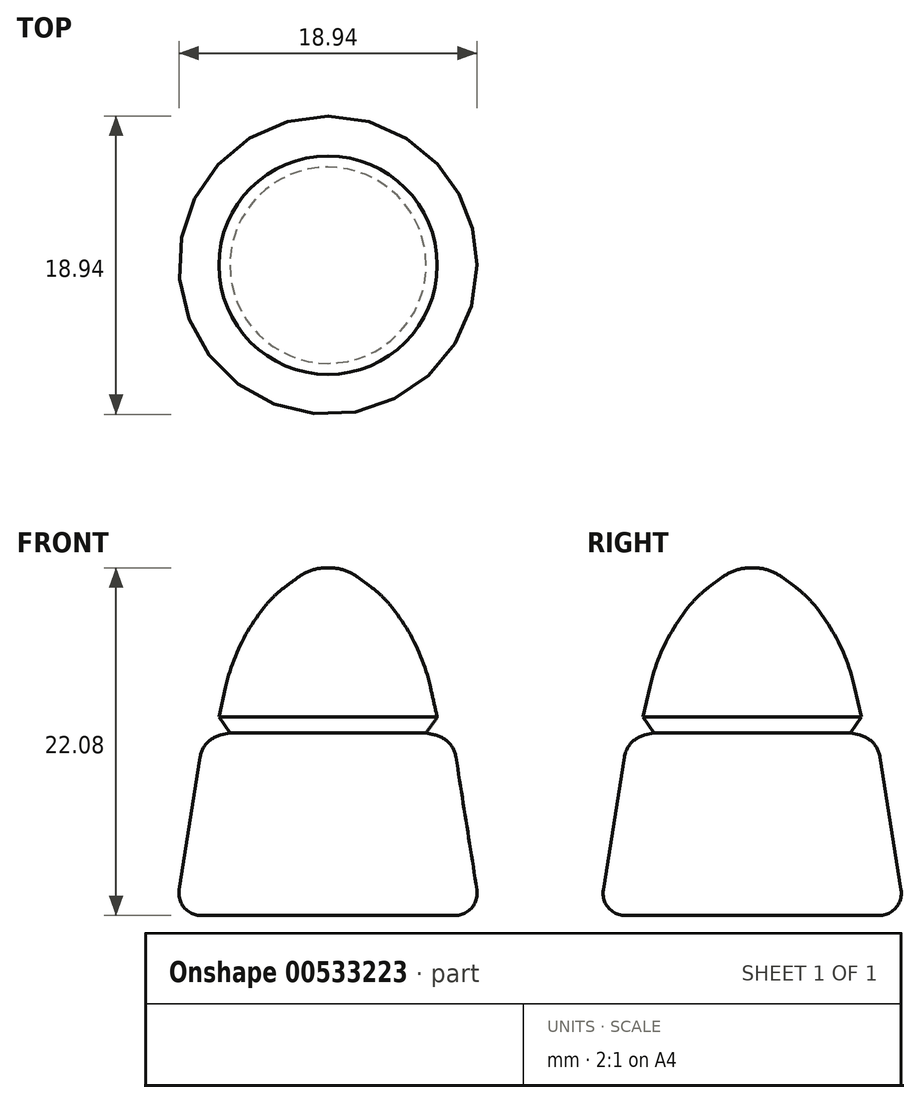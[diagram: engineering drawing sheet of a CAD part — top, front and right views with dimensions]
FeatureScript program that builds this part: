
annotation { "Feature Type Name" : "Feature", "Feature Type Description" : "" }
export const myFeature = defineFeature(function(context is Context, id is Id, definition is map)
    precondition{}
    {
        {
            var Q0;
            Q0=qCreatedBy(makeId("Front.planeOp"),FACE);
            var sketch = newSketch(context, id + "F0", { "sketchPlane" : qUnion([Q0])});
            skLineSegment(sketch, "E0", {"start": v(0, 0) * mm, "end": v(-9.71, 0) * mm});
            skLineSegment(sketch, "E1", {"start": v(-9.71, 0) * mm, "end": v(-7.94, 11.19) * mm});
            skLineSegment(sketch, "E2", {"start": v(-7.94, 11.19) * mm, "end": v(-6.23, 11.6) * mm});
            skLineSegment(sketch, "E3", {"start": v(-6.23, 11.6) * mm, "end": v(-6.94, 12.6) * mm});
            skLineSegment(sketch, "E4", {"start": v(-6.94, 12.6) * mm, "end": v(-5.83, 17.44) * mm});
            skLineSegment(sketch, "E5", {"start": v(-5.83, 17.44) * mm, "end": v(-3.4, 20.36) * mm});
            skLineSegment(sketch, "E6", {"start": v(-3.4, 20.36) * mm, "end": v(-1.09, 22.08) * mm});
            skLineSegment(sketch, "E7", {"start": v(-1.09, 22.08) * mm, "end": v(0, 22.08) * mm});
            skLineSegment(sketch, "E8", {"start": v(0, 22.08) * mm, "end": v(0, 0) * mm});
            skSolve(sketch);
        }
        {
            var Q0;
            Q0=makeQuery(id+"F0.imprint","IMPRINT",FACE,{"disambiguationData":[TD([[makeQuery(id+"F0.imprint","IMPRINT",EDGE,{"derivedFrom":sQuery(id+"F0.wireOp",EDGE,"E0")}),-1.0]])]});
            var Q1;
            Q1=sQuery(id+"F0.wireOp",EDGE,"E8");
            revolve(context, id + "F1", {"entities" : qUnion([Q0]), "axis" : qUnion([Q1]), "revolveType" : RevolveType.FULL});
        }
        {
            var Q0;
            Q0=makeQuery(id+"F1.opRevolve","SWEPT_EDGE",EDGE,{"disambiguationData":[OSD([sQuery(id+"F0.wireOp",EDGE,"E4"),sQuery(id+"F0.wireOp",EDGE,"E5")])]});
            fillet(context, id + "F2", {"entities" : qUnion([Q0]), "radius" : 12.6 * mm, "tangentPropagation" : true, "allowEdgeOverflow" : false});
        }
        {
            var Q0;
            Q0=makeQuery(id+"F1.opRevolve","SWEPT_EDGE",EDGE,{"disambiguationData":[OSD([sQuery(id+"F0.wireOp",EDGE,"E5"),sQuery(id+"F0.wireOp",EDGE,"E6")])]});
            fillet(context, id + "F3", {"entities" : qUnion([Q0]), "radius" : 6.74 * mm, "tangentPropagation" : true, "allowEdgeOverflow" : false});
        }
        {
            var Q0;
            Q0=makeQuery(id+"F1.opRevolve","SWEPT_EDGE",EDGE,{"disambiguationData":[OSD([sQuery(id+"F0.wireOp",EDGE,"E6"),sQuery(id+"F0.wireOp",EDGE,"E7")])]});
            fillet(context, id + "F4", {"entities" : qUnion([Q0]), "radius" : 3.03 * mm, "tangentPropagation" : true, "allowEdgeOverflow" : false});
        }
        {
            var Q0;
            Q0=makeQuery(id+"F1.opRevolve","SWEPT_EDGE",EDGE,{"disambiguationData":[OSD([sQuery(id+"F0.wireOp",EDGE,"E1"),sQuery(id+"F0.wireOp",EDGE,"E2")])]});
            fillet(context, id + "F5", {"entities" : qUnion([Q0]), "radius" : 1.71 * mm, "tangentPropagation" : true, "allowEdgeOverflow" : false});
        }
        {
            var Q0;
            Q0=makeQuery(id+"F1.opRevolve","SWEPT_EDGE",EDGE,{"disambiguationData":[OSD([sQuery(id+"F0.wireOp",EDGE,"E0"),sQuery(id+"F0.wireOp",EDGE,"E1")])]});
            fillet(context, id + "F6", {"entities" : qUnion([Q0]), "radius" : 1.4 * mm, "tangentPropagation" : true, "allowEdgeOverflow" : false});
        }
    });
